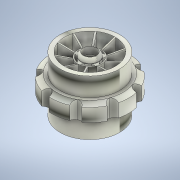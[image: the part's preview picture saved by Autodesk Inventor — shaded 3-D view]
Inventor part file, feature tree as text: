
AUTODESK INVENTOR PART (.ipt)
format: ipt  version: 2022 (Build 260153000, 153)  size: 531,968 bytes
history: native  units: mm
features: chamfer x28, extrude x13, sketch x13, fillet x1
ambient origin geometry x8: Origin, YZ Plane, XZ Plane, XY Plane, X Axis, Y Axis, Z Axis, Center Point
bodies: Solid1 (feature_tree)
feature tree (55):
  extrude  "Extrusion1"  Depth=8.5mm TaperAngle=0.0deg
  extrude  "Extrusion2"  Depth=8.5mm TaperAngle=0.0deg
  extrude  "Extrusion3"  Depth=2.0mm
  extrude  "Extrusion4"  Depth=8.5mm
  chamfer  "Chamfer1"  Distance=90.0mm Angle=360.0deg
  chamfer  "Chamfer2"  Distance=8.5mm
  chamfer  "Chamfer3"  Distance=2.5mm Angle=45.0deg
  chamfer  "Chamfer4"  Distance=2.5mm Angle=45.0deg
  chamfer  "Chamfer5"  Distance=2.5mm Angle=45.0deg
  chamfer  "Chamfer6"  Distance=2.5mm Angle=45.0deg
  chamfer  "Chamfer7"  Distance=2.5mm Angle=45.0deg
  chamfer  "Chamfer8"  Distance=2.5mm Angle=45.0deg
  chamfer  "Chamfer9"  Distance=2.5mm Angle=45.0deg
  chamfer  "Chamfer10"  Distance=2.5mm Angle=45.0deg
  chamfer  "Chamfer11"  Distance=2.5mm Angle=45.0deg
  chamfer  "Chamfer12"  Distance=1.0mm Angle=45.0deg
  chamfer  "Chamfer13"  Distance=1.0mm Angle=45.0deg
  chamfer  "Chamfer14"  Distance=1.0mm Angle=45.0deg
  chamfer  "Chamfer15"  Distance=1.0mm Angle=45.0deg
  chamfer  "Chamfer16"  Distance=1.0mm Angle=45.0deg
  chamfer  "Chamfer17"  Distance=1.0mm Angle=45.0deg
  chamfer  "Chamfer18"  Distance=1.0mm Angle=45.0deg
  extrude  "Extrusion5"  Depth=1.0mm TaperAngle=45.0deg
  extrude  "Extrusion6"  Depth=8.5mm TaperAngle=0.0deg
  extrude  "Extrusion7"  Depth=8.5mm TaperAngle=0.0deg
  extrude  "Extrusion8"  Depth=3.2mm TaperAngle=0.0deg
  extrude  "Extrusion9"  Depth=5.0mm TaperAngle=0.0deg
  extrude  "Extrusion10"  Depth=2.3mm
  extrude  "Extrusion11"  Depth=2.0mm
  extrude  "Extrusion12"  Depth=100.0mm TaperAngle=360.0deg
  fillet  "Fillet2"  Radius=0.5mm
  chamfer  "Chamfer20"  Distance=50.0mm Angle=360.0deg
  chamfer  "Chamfer21"  [1 undecoded]
  chamfer  "Chamfer22"  Distance=2.0mm
  chamfer  "Chamfer23"  Distance=6.0mm Angle=45.0deg
  chamfer  "Chamfer24"  Distance=6.0mm Angle=45.0deg
  chamfer  "Chamfer25"  Distance=6.0mm Angle=45.0deg
  chamfer  "Chamfer26"  Distance=6.0mm Angle=45.0deg
  chamfer  "Chamfer27"  Distance=6.0mm Angle=45.0deg
  chamfer  "Chamfer28"  Distance=6.0mm Angle=45.0deg
  chamfer  "Chamfer29"  Distance=6.0mm Angle=45.0deg
  extrude  "Extrusion13"  Depth=5.0mm TaperAngle=45.0deg
  sketch  "Sketch1"  dims[d0=15.0mm d1=8.5mm d2=0.0mm]
  sketch  "Sketch2"  dims[d4=8.0mm d5=0.0mm d6=8.5mm d7=0.0mm]
  sketch  "Sketch3"  dims[d10=2.5mm d11=2.0mm]
  sketch  "Sketch5"  dims[d12=2.0mm d14=12.361mm d15=90.0mm d17=360.0deg d19=8.5mm d20=0.0mm d21=2.5mm d22=1.0mm d23=45.0deg d24=2.5mm d25=1.0mm d26=45.0deg d27=2.5mm d28=1.0mm d29=45.0deg d30=2.5mm d31=1.0mm d32=45.0deg d33=2.5mm d34=1.0mm d35=45.0deg d36=2.5mm d37=1.0mm d38=45.0deg d39=2.5mm d40=1.0mm d41=45.0deg d42=2.5mm d43=1.0mm d44=45.0deg d45=2.5mm d46=1.0mm d47=45.0deg d48=1.0mm d49=2.5mm d50=45.0deg d51=1.0mm d52=2.5mm d53=45.0deg d54=1.0mm d55=2.5mm d56=45.0deg d57=1.0mm d58=2.5mm d59=45.0deg d60=1.0mm d61=2.5mm d62=45.0deg d63=1.0mm d64=2.5mm d65=45.0deg d66=1.0mm d67=2.5mm d68=45.0deg]
  sketch  "Sketch6"  dims[d69=1.0mm d70=2.5mm d71=45.0deg d72=1.0mm d73=2.5mm d74=45.0deg]
  sketch  "Sketch7"  dims[d75=1.5mm d76=8.5mm d77=0.0mm]
  sketch  "Sketch8"  dims[d78=1.5mm d79=8.5mm d80=0.0mm]
  sketch  "Sketch9"  dims[d81=6.0mm d82=3.2mm d83=0.0mm]
  sketch  "Sketch10"  dims[d84=4.0mm d85=5.0mm d86=0.0mm]
  sketch  "Sketch11"  dims[d88=6.0mm d89=0.0mm d90=2.3mm]
  sketch  "Sketch12"  dims[d91=0.0mm d92=0.0mm d93=2.0mm]
  sketch  "Sketch13"  dims[d96=5.5mm d97=100.0mm d99=360.0deg d101=0.5mm d102=50.0mm d104=360.0deg d106=0.0mm d107=0.0mm d108=2.0mm d109=0.0mm]
  sketch  "Sketch14"  dims[d114=2.0mm d115=6.0mm d116=2.0mm d117=45.0deg d118=6.0mm d119=2.0mm d120=45.0deg d121=6.0mm d122=2.0mm d123=45.0deg d124=6.0mm d125=2.0mm d126=45.0deg d127=6.0mm d128=2.0mm d129=45.0deg d130=6.0mm d131=2.0mm d132=45.0deg d133=6.0mm d134=2.0mm d135=45.0deg d136=6.0mm d137=2.0mm d138=45.0deg d139=6.0mm d140=2.0mm d141=45.0deg d142=6.0mm d143=2.0mm d144=45.0deg d145=5.5mm d146=5.0mm d147=0.0mm]
note: 1 required parameter value undecoded (feature->parameter linkage not recoverable at this tier; creation-order binding heuristic only, values carry confidence <= 0.55)
